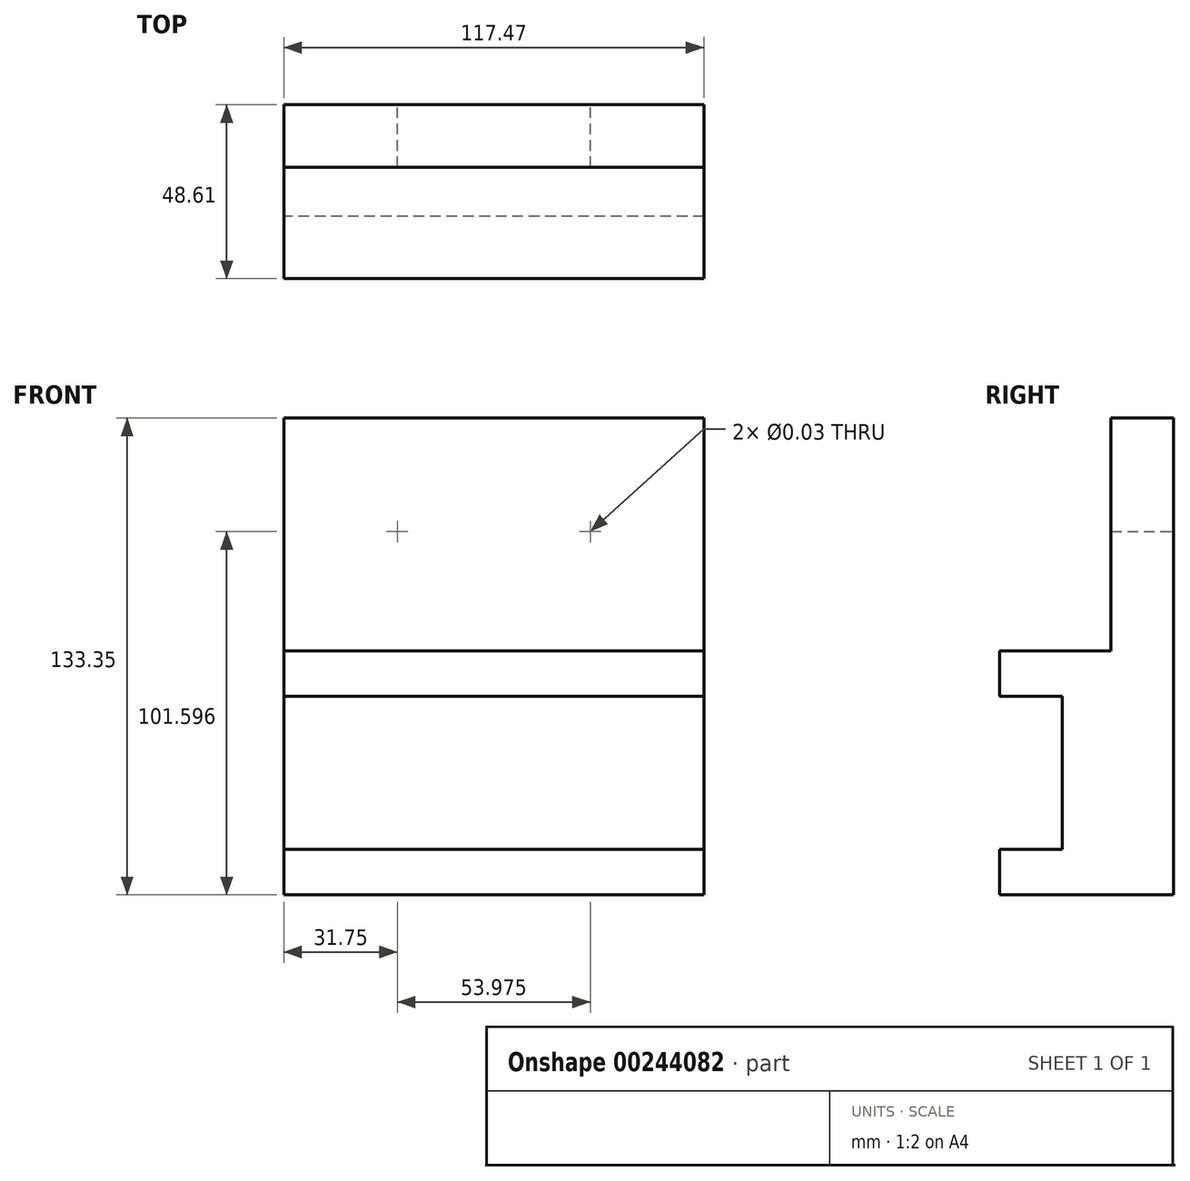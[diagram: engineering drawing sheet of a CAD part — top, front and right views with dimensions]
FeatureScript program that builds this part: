
annotation { "Feature Type Name" : "Feature", "Feature Type Description" : "" }
export const myFeature = defineFeature(function(context is Context, id is Id, definition is map)
    precondition{}
    {
        {
            var Q0;
            Q0=qCreatedBy(makeId("Right.planeOp"),FACE);
            var sketch = newSketch(context, id + "F0", { "sketchPlane" : qUnion([Q0])});
            skLineSegment(sketch, "E0", {"start": v(-51.17, 182.64) * mm, "end": v(-51.17, 49.29) * mm});
            skLineSegment(sketch, "E1", {"start": v(-51.17, 182.64) * mm, "end": v(-68.63, 182.64) * mm});
            skLineSegment(sketch, "E2", {"start": v(-82.32, 61.99) * mm, "end": v(-82.32, 104.85) * mm});
            skLineSegment(sketch, "E3", {"start": v(-82.32, 104.85) * mm, "end": v(-99.78, 104.85) * mm});
            skLineSegment(sketch, "E4", {"start": v(-99.78, 104.85) * mm, "end": v(-99.78, 117.55) * mm});
            skLineSegment(sketch, "E5", {"start": v(-99.78, 117.55) * mm, "end": v(-68.63, 117.55) * mm});
            skLineSegment(sketch, "E6", {"start": v(-68.63, 117.55) * mm, "end": v(-68.63, 182.64) * mm});
            skLineSegment(sketch, "E7", {"start": v(-68.63, 117.55) * mm, "end": v(-68.63, 49.29) * mm});
            skLineSegment(sketch, "E8", {"start": v(-51.17, 49.29) * mm, "end": v(-99.78, 49.29) * mm});
            skLineSegment(sketch, "E9", {"start": v(-99.78, 49.29) * mm, "end": v(-99.78, 61.99) * mm});
            skLineSegment(sketch, "E10", {"start": v(-82.32, 61.99) * mm, "end": v(-99.78, 61.99) * mm});
            skSolve(sketch);
        }
        {
            var Q0;
            Q0 = qSketchRegion(id + "F0", true);
            extrude(context, id + "F1", {"entities" : qUnion([Q0]), "depth" : 117.47 * mm});
        }
        {
            var Q0;
            Q0=qCreatedBy(makeId("Front.planeOp"),FACE);
            var sketch = newSketch(context, id + "F2", { "sketchPlane" : qUnion([Q0])});
            skLineSegment(sketch, "E11", {"start": v(6.99, 150.89) * mm, "end": v(138.17, 150.89) * mm});
            skLineSegment(sketch, "E12", {"start": v(85.72, 188.97) * mm, "end": v(85.72, 131.76) * mm});
            skLineSegment(sketch, "E13", {"start": v(31.75, 189.27) * mm, "end": v(31.75, 129.07) * mm});
            skPoint(sketch, "E14", {"position": v(31.75, 150.89) * mm});
            skPoint(sketch, "E15", {"position": v(85.72, 150.89) * mm});
            skSolve(sketch);
        }
        {
            var Q0;
            Q0=sQuery(id+"F2.wireOp",VERTEX,"E14");
            var Q1;
            Q1=sQuery(id+"F2.wireOp",VERTEX,"E15");
            var Q2;
            Q2=makeQuery(id+"F1.opExtrude","SWEPT_BODY",BODY,{"disambiguationData":[OSD([sQuery(id+"F0.wireOp",EDGE,"E0"),sQuery(id+"F0.wireOp",EDGE,"E1"),sQuery(id+"F0.wireOp",EDGE,"E2"),sQuery(id+"F0.wireOp",EDGE,"E3"),sQuery(id+"F0.wireOp",EDGE,"E4"),sQuery(id+"F0.wireOp",EDGE,"E5"),sQuery(id+"F0.wireOp",EDGE,"E6"),sQuery(id+"F0.wireOp",EDGE,"E8"),sQuery(id+"F0.wireOp",EDGE,"E9"),sQuery(id+"F0.wireOp",EDGE,"E10")])]});
            hole(context, id + "F3", {"style" : HoleStyle.SIMPLE, "endStyle" : HoleEndStyle.THROUGH, "oppositeDirection" : true, "holeDiameter" : 13 / 406.4 * mm, "tappedDepth" : 12.7 * mm, "tapClearance" : 3, "locations" : qUnion([Q0, Q1]), "scope" : qUnion([Q2])});
        }
    });
